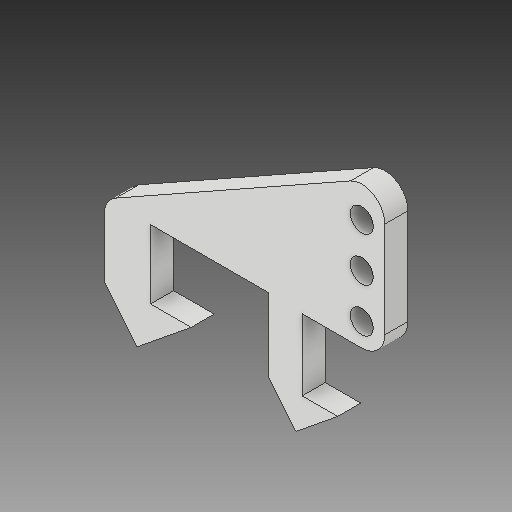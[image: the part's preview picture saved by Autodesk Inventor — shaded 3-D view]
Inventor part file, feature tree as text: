
AUTODESK INVENTOR PART (.ipt)
format: ipt  version: 2017 (Build 210142000, 142)  size: 119,296 bytes
history: native  units: in
note: dims shown in document units (in); Inventor stores cm internally (conversion verified against a paired STEP export)
features: other x3, sketch x1
ambient origin geometry x8: Origin, YZ Plane, XZ Plane, XY Plane, X Axis, Y Axis, Z Axis, Center Point
bodies: Solid1 (feature_tree)
feature tree (4):
  other  "horn.ipt"
  other  "Solid1::horn.ipt"
  other  "TaggingFeature1"
  sketch  "Sketch1"  dims[d0=0.3937in]
